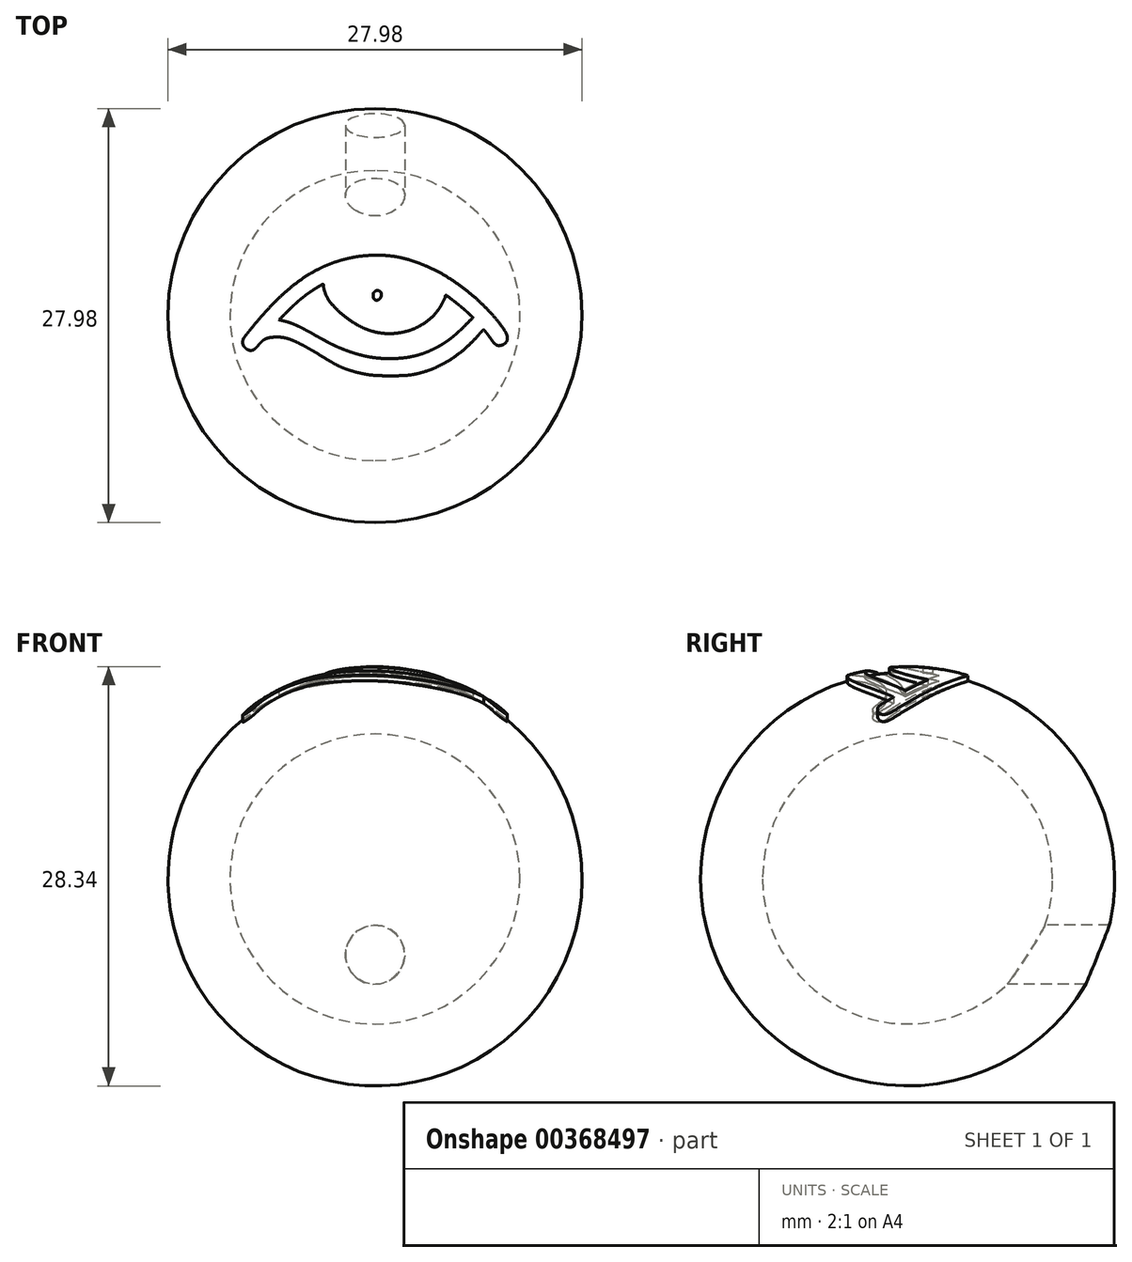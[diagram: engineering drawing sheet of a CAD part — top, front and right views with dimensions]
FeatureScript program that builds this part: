
annotation { "Feature Type Name" : "Feature", "Feature Type Description" : "" }
export const myFeature = defineFeature(function(context is Context, id is Id, definition is map)
    precondition{}
    {
        {
            var Q0;
            Q0=qCreatedBy(makeId("Top.planeOp"),FACE);
            var sketch = newSketch(context, id + "F0", { "sketchPlane" : qUnion([Q0])});
            skLineSegment(sketch, "E0", {"start": v(0, -10) * mm, "end": v(0, 10) * mm});
            skArc(sketch, "E1", {"start": v(0, 10) * mm, "mid": v(-10, 0) * mm, "end": v(0, -10) * mm});
            skSolve(sketch);
        }
        {
            var Q0;
            {var subQ0=sQuery(id+"F0.wireOp",EDGE,"E1");Q0=makeQuery(id+"F0.imprint","IMPRINT",FACE,{"disambiguationData":[TD([[makeQuery(id+"F0.imprint","IMPRINT",EDGE,{"derivedFrom":subQ0}),1.0]])]});}
            var Q1;
            Q1=sQuery(id+"F0.wireOp",EDGE,"E0");
            revolve(context, id + "F1", {"entities" : qUnion([Q0]), "axis" : qUnion([Q1]), "revolveType" : RevolveType.FULL});
        }
        {
            var Q0;
            Q0=makeQuery(id+"F1.opRevolve","SWEPT_BODY",BODY,{"disambiguationData":[OSD([sQuery(id+"F0.wireOp",EDGE,"E0"),sQuery(id+"F0.wireOp",EDGE,"E1")])]});
            var Q1;
            Q1=sQuery(id+"F0.wireOp",VERTEX,"NPe4G0ez-t7S9-9isL-QO5v-uuJu600mHcIT.center");
            var Q2;
            Q2=sQuery(id+"F0.wireOp",VERTEX,"E1.center");
            transform(context, id + "F2", {"entities" : qUnion([Q0]), "transformType" : TransformType.SCALE_UNIFORMLY, "scale" : 33.3, "scalePoint" : qUnion([Q2]), "makeCopy" : false});
        }
        {
            var Q0;
            Q0=qCreatedBy(makeId("Top.planeOp"),FACE);
            var sketch = newSketch(context, id + "F3", { "sketchPlane" : qUnion([Q0])});
            skArc(sketch, "E2", {"start": v(-15.7, 96.27) * mm, "mid": v(-24.88, 95.28) * mm, "end": v(-34, 93.81) * mm});
            skArc(sketch, "E3", {"start": v(-34, 93.81) * mm, "mid": v(-43.55, 91.8) * mm, "end": v(-53.01, 89.37) * mm});
            skArc(sketch, "E4", {"start": v(-53.01, 89.37) * mm, "mid": v(-62.4, 86.52) * mm, "end": v(-71.64, 83.27) * mm});
            skArc(sketch, "E5", {"start": v(-71.64, 83.27) * mm, "mid": v(-80.3, 79.75) * mm, "end": v(-88.77, 75.81) * mm});
            skArc(sketch, "E6", {"start": v(-88.77, 75.81) * mm, "mid": v(-102.81, 68.2) * mm, "end": v(-116.28, 59.63) * mm});
            skArc(sketch, "E7", {"start": v(-116.28, 59.63) * mm, "mid": v(-129.86, 49.68) * mm, "end": v(-142.83, 38.92) * mm});
            skArc(sketch, "E8", {"start": v(-142.83, 38.92) * mm, "mid": v(-156.87, 25.88) * mm, "end": v(-170.22, 12.13) * mm});
            skArc(sketch, "E9", {"start": v(-170.22, 12.13) * mm, "mid": v(-185.55, -5) * mm, "end": v(-200.36, -22.6) * mm});
            skArc(sketch, "E10", {"start": v(-200.36, -22.6) * mm, "mid": v(-204.26, -27.4) * mm, "end": v(-208.11, -32.22) * mm});
            skArc(sketch, "E11", {"start": v(-208.11, -32.22) * mm, "mid": v(-209.68, -34.33) * mm, "end": v(-211.1, -36.54) * mm});
            skArc(sketch, "E12", {"start": v(-211.1, -36.54) * mm, "mid": v(-211.9, -38.1) * mm, "end": v(-212.43, -39.77) * mm});
            skArc(sketch, "E13", {"start": v(-212.43, -39.77) * mm, "mid": v(-212.77, -41.62) * mm, "end": v(-212.89, -43.5) * mm});
            skArc(sketch, "E14", {"start": v(-212.89, -43.5) * mm, "mid": v(-212.7, -45.36) * mm, "end": v(-212.17, -47.16) * mm});
            skArc(sketch, "E15", {"start": v(-212.17, -47.16) * mm, "mid": v(-211.25, -49.03) * mm, "end": v(-210.08, -50.75) * mm});
            skArc(sketch, "E16", {"start": v(-210.08, -50.75) * mm, "mid": v(-208.63, -52.35) * mm, "end": v(-206.98, -53.74) * mm});
            skArc(sketch, "E17", {"start": v(-206.98, -53.74) * mm, "mid": v(-205.23, -54.82) * mm, "end": v(-203.34, -55.62) * mm});
            skArc(sketch, "E18", {"start": v(-203.34, -55.62) * mm, "mid": v(-201.34, -56.09) * mm, "end": v(-199.3, -56.2) * mm});
            skArc(sketch, "E19", {"start": v(-199.3, -56.2) * mm, "mid": v(-197.43, -55.94) * mm, "end": v(-195.66, -55.27) * mm});
            skArc(sketch, "E20", {"start": v(-195.66, -55.27) * mm, "mid": v(-193.67, -54.05) * mm, "end": v(-191.9, -52.53) * mm});
            skArc(sketch, "E21", {"start": v(-191.9, -52.53) * mm, "mid": v(-189.54, -50.04) * mm, "end": v(-187.31, -47.43) * mm});
            skArc(sketch, "E22", {"start": v(-187.31, -47.43) * mm, "mid": v(-184.58, -44.29) * mm, "end": v(-181.61, -41.36) * mm});
            skArc(sketch, "E23", {"start": v(-181.61, -41.36) * mm, "mid": v(-179.01, -39.32) * mm, "end": v(-176.14, -37.68) * mm});
            skArc(sketch, "E24", {"start": v(-176.14, -37.68) * mm, "mid": v(-172.97, -36.44) * mm, "end": v(-169.65, -35.65) * mm});
            skArc(sketch, "E25", {"start": v(-169.65, -35.65) * mm, "mid": v(-165.2, -35.07) * mm, "end": v(-160.72, -34.76) * mm});
            skArc(sketch, "E26", {"start": v(-160.72, -34.76) * mm, "mid": v(-158.15, -34.7) * mm, "end": v(-155.59, -34.7) * mm});
            skArc(sketch, "E27", {"start": v(-155.59, -34.7) * mm, "mid": v(-153.46, -34.78) * mm, "end": v(-151.33, -34.94) * mm});
            skArc(sketch, "E28", {"start": v(-151.33, -34.94) * mm, "mid": v(-149.29, -35.18) * mm, "end": v(-147.26, -35.51) * mm});
            skArc(sketch, "E29", {"start": v(-147.26, -35.51) * mm, "mid": v(-144.98, -35.98) * mm, "end": v(-142.72, -36.5) * mm});
            skArc(sketch, "E30", {"start": v(-142.72, -36.5) * mm, "mid": v(-137.7, -37.98) * mm, "end": v(-132.83, -39.85) * mm});
            skArc(sketch, "E31", {"start": v(-132.83, -39.85) * mm, "mid": v(-126.18, -42.83) * mm, "end": v(-119.62, -46) * mm});
            skArc(sketch, "E32", {"start": v(-119.62, -46) * mm, "mid": v(-111.94, -50) * mm, "end": v(-104.36, -54.22) * mm});
            skArc(sketch, "E33", {"start": v(-104.36, -54.22) * mm, "mid": v(-96.08, -59.09) * mm, "end": v(-87.89, -64.12) * mm});
            skArc(sketch, "E34", {"start": v(-87.89, -64.12) * mm, "mid": v(-78.64, -69.83) * mm, "end": v(-69.3, -75.4) * mm});
            skArc(sketch, "E35", {"start": v(-69.3, -75.4) * mm, "mid": v(-62.78, -79.02) * mm, "end": v(-56.09, -82.33) * mm});
            skArc(sketch, "E36", {"start": v(-56.09, -82.33) * mm, "mid": v(-50.08, -84.92) * mm, "end": v(-43.94, -87.15) * mm});
            skArc(sketch, "E37", {"start": v(-43.94, -87.15) * mm, "mid": v(-36.7, -89.4) * mm, "end": v(-29.39, -91.38) * mm});
            skArc(sketch, "E38", {"start": v(-29.39, -91.38) * mm, "mid": v(-22.75, -92.95) * mm, "end": v(-16.08, -94.33) * mm});
            skArc(sketch, "E39", {"start": v(-16.08, -94.33) * mm, "mid": v(-10.4, -95.3) * mm, "end": v(-4.68, -96.02) * mm});
            skArc(sketch, "E40", {"start": v(-4.68, -96.02) * mm, "mid": v(1.7, -96.55) * mm, "end": v(8.07, -96.83) * mm});
            skArc(sketch, "E41", {"start": v(8.07, -96.83) * mm, "mid": v(17.1, -97) * mm, "end": v(26.11, -97.06) * mm});
            skArc(sketch, "E42", {"start": v(26.11, -97.06) * mm, "mid": v(34.81, -96.98) * mm, "end": v(43.5, -96.78) * mm});
            skArc(sketch, "E43", {"start": v(43.5, -96.78) * mm, "mid": v(49.38, -96.48) * mm, "end": v(55.24, -95.93) * mm});
            skArc(sketch, "E44", {"start": v(55.24, -95.93) * mm, "mid": v(60.42, -95.18) * mm, "end": v(65.57, -94.17) * mm});
            skArc(sketch, "E45", {"start": v(65.57, -94.17) * mm, "mid": v(71.73, -92.68) * mm, "end": v(77.85, -91.01) * mm});
            skArc(sketch, "E46", {"start": v(77.85, -91.01) * mm, "mid": v(89.65, -87.08) * mm, "end": v(101.1, -82.22) * mm});
            skArc(sketch, "E47", {"start": v(101.1, -82.22) * mm, "mid": v(112.52, -76.3) * mm, "end": v(123.5, -69.56) * mm});
            skArc(sketch, "E48", {"start": v(123.5, -69.56) * mm, "mid": v(134.48, -61.7) * mm, "end": v(144.89, -53.1) * mm});
            skArc(sketch, "E49", {"start": v(144.89, -53.1) * mm, "mid": v(155.3, -43.34) * mm, "end": v(165.12, -32.98) * mm});
            skLineSegment(sketch, "E50", {"start": v(165.12, -32.98) * mm, "end": v(174.6, -22.4) * mm});
            skLineSegment(sketch, "E51", {"start": v(174.6, -22.4) * mm, "end": v(177.93, -26.25) * mm});
            skArc(sketch, "E52", {"start": v(177.93, -26.25) * mm, "mid": v(178.76, -27.23) * mm, "end": v(179.56, -28.24) * mm});
            skArc(sketch, "E53", {"start": v(179.56, -28.24) * mm, "mid": v(180.69, -29.73) * mm, "end": v(181.8, -31.22) * mm});
            skArc(sketch, "E54", {"start": v(181.8, -31.22) * mm, "mid": v(183.01, -32.88) * mm, "end": v(184.21, -34.54) * mm});
            skArc(sketch, "E55", {"start": v(184.21, -34.54) * mm, "mid": v(185.33, -36.15) * mm, "end": v(186.44, -37.76) * mm});
            skArc(sketch, "E56", {"start": v(186.44, -37.76) * mm, "mid": v(188.89, -41.17) * mm, "end": v(191.53, -44.43) * mm});
            skArc(sketch, "E57", {"start": v(191.53, -44.43) * mm, "mid": v(193.5, -46.3) * mm, "end": v(195.78, -47.72) * mm});
            skArc(sketch, "E58", {"start": v(195.78, -47.72) * mm, "mid": v(197.94, -48.43) * mm, "end": v(200.2, -48.52) * mm});
            skArc(sketch, "E59", {"start": v(200.2, -48.52) * mm, "mid": v(202.97, -48.04) * mm, "end": v(205.62, -47.16) * mm});
            skArc(sketch, "E60", {"start": v(205.62, -47.16) * mm, "mid": v(208.3, -45.62) * mm, "end": v(210.53, -43.46) * mm});
            skArc(sketch, "E61", {"start": v(210.53, -43.46) * mm, "mid": v(212.04, -40.9) * mm, "end": v(212.79, -38.01) * mm});
            skArc(sketch, "E62", {"start": v(212.79, -38.01) * mm, "mid": v(212.79, -34.58) * mm, "end": v(212.02, -31.24) * mm});
            skArc(sketch, "E63", {"start": v(212.02, -31.24) * mm, "mid": v(210.38, -27.4) * mm, "end": v(208.26, -23.82) * mm});
            skArc(sketch, "E64", {"start": v(208.26, -23.82) * mm, "mid": v(196.57, -8.01) * mm, "end": v(183.65, 6.8) * mm});
            skArc(sketch, "E65", {"start": v(183.65, 6.8) * mm, "mid": v(168.5, 21.85) * mm, "end": v(152.44, 35.92) * mm});
            skArc(sketch, "E66", {"start": v(152.44, 35.92) * mm, "mid": v(135.48, 49) * mm, "end": v(117.73, 60.98) * mm});
            skArc(sketch, "E67", {"start": v(117.73, 60.98) * mm, "mid": v(100.55, 70.9) * mm, "end": v(82.64, 79.43) * mm});
            skArc(sketch, "E68", {"start": v(82.64, 79.43) * mm, "mid": v(70.04, 84.47) * mm, "end": v(57.22, 88.9) * mm});
            skArc(sketch, "E69", {"start": v(57.22, 88.9) * mm, "mid": v(45.56, 92.16) * mm, "end": v(33.7, 94.6) * mm});
            skArc(sketch, "E70", {"start": v(33.7, 94.6) * mm, "mid": v(21.92, 96.2) * mm, "end": v(10.05, 96.96) * mm});
            skArc(sketch, "E71", {"start": v(10.05, 96.96) * mm, "mid": v(-2.83, 96.97) * mm, "end": v(-15.7, 96.27) * mm});
            skArc(sketch, "E72", {"start": v(-82.87, 47.15) * mm, "mid": v(-82.82, 46.3) * mm, "end": v(-82.7, 45.47) * mm});
            skArc(sketch, "E73", {"start": v(-82.7, 45.47) * mm, "mid": v(-82.45, 44.2) * mm, "end": v(-82.17, 42.93) * mm});
            skArc(sketch, "E74", {"start": v(-82.17, 42.93) * mm, "mid": v(-81.8, 41.5) * mm, "end": v(-81.41, 40.08) * mm});
            skArc(sketch, "E75", {"start": v(-81.41, 40.08) * mm, "mid": v(-80.99, 38.7) * mm, "end": v(-80.52, 37.33) * mm});
            skArc(sketch, "E76", {"start": v(-80.52, 37.33) * mm, "mid": v(-75.98, 27.48) * mm, "end": v(-69.69, 18.65) * mm});
            skArc(sketch, "E77", {"start": v(-69.69, 18.65) * mm, "mid": v(-60.18, 8.6) * mm, "end": v(-49.8, -0.55) * mm});
            skArc(sketch, "E78", {"start": v(-49.8, -0.55) * mm, "mid": v(-38.08, -9.14) * mm, "end": v(-25.64, -16.65) * mm});
            skArc(sketch, "E79", {"start": v(-25.64, -16.65) * mm, "mid": v(-13.91, -22.11) * mm, "end": v(-1.6, -26.06) * mm});
            skArc(sketch, "E80", {"start": v(-1.6, -26.06) * mm, "mid": v(12.82, -28.6) * mm, "end": v(27.45, -29.03) * mm});
            skArc(sketch, "E81", {"start": v(27.45, -29.03) * mm, "mid": v(42.14, -27.34) * mm, "end": v(56.45, -23.6) * mm});
            skArc(sketch, "E82", {"start": v(56.45, -23.6) * mm, "mid": v(69.79, -17.97) * mm, "end": v(82.17, -10.47) * mm});
            skArc(sketch, "E83", {"start": v(82.17, -10.47) * mm, "mid": v(92.73, -1.58) * mm, "end": v(101.67, 8.94) * mm});
            skArc(sketch, "E84", {"start": v(101.67, 8.94) * mm, "mid": v(103.47, 11.6) * mm, "end": v(105.14, 14.32) * mm});
            skArc(sketch, "E85", {"start": v(105.14, 14.32) * mm, "mid": v(107.13, 17.86) * mm, "end": v(109.03, 21.44) * mm});
            skArc(sketch, "E86", {"start": v(109.03, 21.44) * mm, "mid": v(110.8, 24.92) * mm, "end": v(112.5, 28.44) * mm});
            skArc(sketch, "E87", {"start": v(112.5, 28.44) * mm, "mid": v(112.96, 29.75) * mm, "end": v(113.11, 31.12) * mm});
            skArc(sketch, "E88", {"start": v(113.11, 31.12) * mm, "mid": v(113.13, 31.37) * mm, "end": v(113.17, 31.61) * mm});
            skArc(sketch, "E89", {"start": v(113.17, 31.61) * mm, "mid": v(113.24, 31.83) * mm, "end": v(113.34, 32.03) * mm});
            skArc(sketch, "E90", {"start": v(113.34, 32.03) * mm, "mid": v(113.46, 32.18) * mm, "end": v(113.6, 32.3) * mm});
            skArc(sketch, "E91", {"start": v(113.6, 32.3) * mm, "mid": v(113.74, 32.38) * mm, "end": v(113.9, 32.4) * mm});
            skArc(sketch, "E92", {"start": v(113.9, 32.4) * mm, "mid": v(115.02, 32.21) * mm, "end": v(116.02, 31.67) * mm});
            skArc(sketch, "E93", {"start": v(116.02, 31.67) * mm, "mid": v(122.38, 26.73) * mm, "end": v(128.73, 21.77) * mm});
            skArc(sketch, "E94", {"start": v(128.73, 21.77) * mm, "mid": v(134.7, 17.03) * mm, "end": v(140.62, 12.21) * mm});
            skArc(sketch, "E95", {"start": v(140.62, 12.21) * mm, "mid": v(144.67, 8.76) * mm, "end": v(148.6, 5.17) * mm});
            skLineSegment(sketch, "E96", {"start": v(148.6, 5.17) * mm, "end": v(157.59, -3.31) * mm});
            skLineSegment(sketch, "E97", {"start": v(157.59, -3.31) * mm, "end": v(142.6, -18.24) * mm});
            skArc(sketch, "E98", {"start": v(142.6, -18.24) * mm, "mid": v(136.78, -23.9) * mm, "end": v(130.82, -29.4) * mm});
            skArc(sketch, "E99", {"start": v(130.82, -29.4) * mm, "mid": v(125.67, -33.85) * mm, "end": v(120.33, -38.08) * mm});
            skArc(sketch, "E100", {"start": v(120.33, -38.08) * mm, "mid": v(115.17, -41.8) * mm, "end": v(109.84, -45.3) * mm});
            skArc(sketch, "E101", {"start": v(109.84, -45.3) * mm, "mid": v(104.04, -48.75) * mm, "end": v(98.11, -51.97) * mm});
            skArc(sketch, "E102", {"start": v(98.11, -51.97) * mm, "mid": v(90.09, -55.89) * mm, "end": v(81.87, -59.38) * mm});
            skArc(sketch, "E103", {"start": v(81.87, -59.38) * mm, "mid": v(73.97, -62.22) * mm, "end": v(65.92, -64.57) * mm});
            skArc(sketch, "E104", {"start": v(65.92, -64.57) * mm, "mid": v(57.65, -66.43) * mm, "end": v(49.28, -67.79) * mm});
            skArc(sketch, "E105", {"start": v(49.28, -67.79) * mm, "mid": v(40.14, -68.76) * mm, "end": v(30.96, -69.3) * mm});
            skArc(sketch, "E106", {"start": v(30.96, -69.3) * mm, "mid": v(21.95, -69.42) * mm, "end": v(12.94, -69.14) * mm});
            skArc(sketch, "E107", {"start": v(12.94, -69.14) * mm, "mid": v(4.36, -68.5) * mm, "end": v(-4.18, -67.41) * mm});
            skArc(sketch, "E108", {"start": v(-4.18, -67.41) * mm, "mid": v(-12.76, -65.9) * mm, "end": v(-21.27, -63.98) * mm});
            skArc(sketch, "E109", {"start": v(-21.27, -63.98) * mm, "mid": v(-30.29, -61.5) * mm, "end": v(-39.2, -58.7) * mm});
            skArc(sketch, "E110", {"start": v(-39.2, -58.7) * mm, "mid": v(-46.15, -56.25) * mm, "end": v(-53.02, -53.62) * mm});
            skArc(sketch, "E111", {"start": v(-53.02, -53.62) * mm, "mid": v(-59.24, -51.03) * mm, "end": v(-65.37, -48.24) * mm});
            skArc(sketch, "E112", {"start": v(-65.37, -48.24) * mm, "mid": v(-72.4, -44.77) * mm, "end": v(-79.33, -41.12) * mm});
            skArc(sketch, "E113", {"start": v(-79.33, -41.12) * mm, "mid": v(-89.08, -35.75) * mm, "end": v(-98.78, -30.3) * mm});
            skArc(sketch, "E114", {"start": v(-98.78, -30.3) * mm, "mid": v(-106.38, -26.03) * mm, "end": v(-114.04, -21.88) * mm});
            skArc(sketch, "E115", {"start": v(-114.04, -21.88) * mm, "mid": v(-119.86, -18.9) * mm, "end": v(-125.78, -16.1) * mm});
            skArc(sketch, "E116", {"start": v(-125.78, -16.1) * mm, "mid": v(-130.73, -13.97) * mm, "end": v(-135.75, -12.05) * mm});
            skArc(sketch, "E117", {"start": v(-135.75, -12.05) * mm, "mid": v(-140.5, -10.48) * mm, "end": v(-145.33, -9.16) * mm});
            skLineSegment(sketch, "E118", {"start": v(-145.33, -9.16) * mm, "end": v(-154.28, -6.95) * mm});
            skLineSegment(sketch, "E119", {"start": v(-154.28, -6.95) * mm, "end": v(-140.33, 7) * mm});
            skArc(sketch, "E120", {"start": v(-140.33, 7) * mm, "mid": v(-135.38, 11.87) * mm, "end": v(-130.35, 16.68) * mm});
            skArc(sketch, "E121", {"start": v(-130.35, 16.68) * mm, "mid": v(-125.96, 20.72) * mm, "end": v(-121.47, 24.66) * mm});
            skArc(sketch, "E122", {"start": v(-121.47, 24.66) * mm, "mid": v(-117.31, 28.12) * mm, "end": v(-113.07, 31.47) * mm});
            skArc(sketch, "E123", {"start": v(-113.07, 31.47) * mm, "mid": v(-108.85, 34.62) * mm, "end": v(-104.55, 37.63) * mm});
            skArc(sketch, "E124", {"start": v(-104.55, 37.63) * mm, "mid": v(-101.45, 39.71) * mm, "end": v(-98.31, 41.75) * mm});
            skArc(sketch, "E125", {"start": v(-98.31, 41.75) * mm, "mid": v(-94.91, 43.9) * mm, "end": v(-91.49, 46.02) * mm});
            skArc(sketch, "E126", {"start": v(-91.49, 46.02) * mm, "mid": v(-88.18, 48.02) * mm, "end": v(-84.86, 50.02) * mm});
            skArc(sketch, "E127", {"start": v(-84.86, 50.02) * mm, "mid": v(-84.27, 50.28) * mm, "end": v(-83.64, 50.38) * mm});
            skArc(sketch, "E128", {"start": v(-83.64, 50.38) * mm, "mid": v(-83.46, 50.33) * mm, "end": v(-83.34, 50.19) * mm});
            skArc(sketch, "E129", {"start": v(-83.34, 50.19) * mm, "mid": v(-83.2, 49.82) * mm, "end": v(-83.1, 49.44) * mm});
            skArc(sketch, "E130", {"start": v(-83.1, 49.44) * mm, "mid": v(-83, 48.92) * mm, "end": v(-82.93, 48.4) * mm});
            skArc(sketch, "E131", {"start": v(-82.93, 48.4) * mm, "mid": v(-82.88, 47.77) * mm, "end": v(-82.87, 47.15) * mm});
            skArc(sketch, "E132", {"start": v(7.9, 38.84) * mm, "mid": v(8.45, 38.4) * mm, "end": v(8.95, 37.88) * mm});
            skArc(sketch, "E133", {"start": v(8.95, 37.88) * mm, "mid": v(9.33, 37.35) * mm, "end": v(9.63, 36.75) * mm});
            skArc(sketch, "E134", {"start": v(9.63, 36.75) * mm, "mid": v(9.86, 36.04) * mm, "end": v(10, 35.3) * mm});
            skArc(sketch, "E135", {"start": v(10, 35.3) * mm, "mid": v(10.08, 34.3) * mm, "end": v(10.11, 33.3) * mm});
            skArc(sketch, "E136", {"start": v(10.11, 33.3) * mm, "mid": v(9.67, 30.37) * mm, "end": v(8.37, 27.7) * mm});
            skArc(sketch, "E137", {"start": v(8.37, 27.7) * mm, "mid": v(6.42, 25.77) * mm, "end": v(3.9, 24.69) * mm});
            skArc(sketch, "E138", {"start": v(3.9, 24.69) * mm, "mid": v(1.5, 24.73) * mm, "end": v(-0.63, 25.85) * mm});
            skArc(sketch, "E139", {"start": v(-0.63, 25.85) * mm, "mid": v(-2.2, 27.9) * mm, "end": v(-2.9, 30.4) * mm});
            skArc(sketch, "E140", {"start": v(-2.9, 30.4) * mm, "mid": v(-3, 31.9) * mm, "end": v(-3.03, 33.4) * mm});
            skArc(sketch, "E141", {"start": v(-3.03, 33.4) * mm, "mid": v(-2.96, 34.37) * mm, "end": v(-2.77, 35.32) * mm});
            skArc(sketch, "E142", {"start": v(-2.77, 35.32) * mm, "mid": v(-2.47, 36.1) * mm, "end": v(-2.05, 36.83) * mm});
            skArc(sketch, "E143", {"start": v(-2.05, 36.83) * mm, "mid": v(-1.4, 37.63) * mm, "end": v(-0.7, 38.36) * mm});
            skArc(sketch, "E144", {"start": v(-0.7, 38.36) * mm, "mid": v(0.26, 39.13) * mm, "end": v(1.32, 39.75) * mm});
            skArc(sketch, "E145", {"start": v(1.32, 39.75) * mm, "mid": v(2.35, 40.14) * mm, "end": v(3.44, 40.31) * mm});
            skArc(sketch, "E146", {"start": v(3.44, 40.31) * mm, "mid": v(4.56, 40.26) * mm, "end": v(5.64, 40) * mm});
            skArc(sketch, "E147", {"start": v(5.64, 40) * mm, "mid": v(6.8, 39.5) * mm, "end": v(7.9, 38.84) * mm});
            skSolve(sketch);
        }
        {
            var Q0;
            Q0=qSketchRegion(id+"F3",true);
            var Q1;
            Q1=sQuery(id+"F3.wireOp",EDGE,"c928f899-12af-4b01-b412-b3b7da3d830f");
            var Q2;
            Q2=sQuery(id+"F3.wireOp",EDGE,"b69f99c7-a6d0-4d1b-8752-9e82ab4c99ec");
            extrude(context, id + "F4", {"entities" : qUnion([Q0]), "operationType" : NewBodyOperationType.ADD, "surfaceEntities" : qUnion([Q1, Q2]), "depth" : 350 * mm});
        }
        {
            var Q0;
            Q0=makeQuery(id+"F4.opExtrude","SWEPT_BODY",BODY,{"disambiguationData":[OSD([sQuery(id+"F3.wireOp",EDGE,"15c6da4e-992d-4824-9d20-70d2d6be9970"),sQuery(id+"F3.wireOp",EDGE,"268c69ec-46be-456f-85eb-69decc32fe39"),sQuery(id+"F3.wireOp",EDGE,"1d386307-6059-4203-bca6-0c1cec3c82e1"),sQuery(id+"F3.wireOp",EDGE,"7d7c66d2-f869-427f-806b-ad436cacd60e"),sQuery(id+"F3.wireOp",EDGE,"1db91850-860e-493f-a3af-7a0f3f1512ae"),sQuery(id+"F3.wireOp",EDGE,"2c65f23b-9f03-4f6f-ab37-de452af29e3c"),sQuery(id+"F3.wireOp",EDGE,"ba006cbc-bbd7-44d9-84cc-9cde0967c280"),sQuery(id+"F3.wireOp",EDGE,"ae950208-c781-4a25-8fcf-ffe59b9085ff"),sQuery(id+"F3.wireOp",EDGE,"3cce0944-c62d-4831-9b9d-d1a418d328b4"),sQuery(id+"F3.wireOp",EDGE,"9edc5e7d-16c0-40c4-98ad-6b91d5df0e78"),sQuery(id+"F3.wireOp",EDGE,"aa452f44-44a2-4c64-bff5-a2a639df00db"),sQuery(id+"F3.wireOp",EDGE,"16259f99-ce20-4b7b-81e1-fa0909c03eb4"),sQuery(id+"F3.wireOp",EDGE,"79895566-a943-429d-b257-d76af3645bdf"),sQuery(id+"F3.wireOp",EDGE,"a85490ef-f17e-45c8-b92b-28215162778a"),sQuery(id+"F3.wireOp",EDGE,"322f1036-a6fd-4992-ab69-5919540af7a6"),sQuery(id+"F3.wireOp",EDGE,"0a87ff38-4ab4-4140-b3c3-2d7501d9f3b1"),sQuery(id+"F3.wireOp",EDGE,"a6e7bdf2-ef3e-49d4-9b3c-e34f5a41e0c4"),sQuery(id+"F3.wireOp",EDGE,"3e588790-576f-47c1-9730-f5e27fa1e8f9"),sQuery(id+"F3.wireOp",EDGE,"ce3739ef-15fd-4754-ad9c-ccf511a9a8fb"),sQuery(id+"F3.wireOp",EDGE,"201134a3-66f3-4a3f-aa9b-76948966efc0"),sQuery(id+"F3.wireOp",EDGE,"65b511ea-0759-428d-8070-88e1f521d8ea"),sQuery(id+"F3.wireOp",EDGE,"c37cddb6-5cf8-4891-aff4-7191a72080b9"),sQuery(id+"F3.wireOp",EDGE,"52a43dbd-e952-43e1-be3d-d70e107260e6"),sQuery(id+"F3.wireOp",EDGE,"08c1271f-f5c3-4f26-be27-7f5e21217dff"),sQuery(id+"F3.wireOp",EDGE,"59a09f58-0503-4180-962a-e04db21f0da8"),sQuery(id+"F3.wireOp",EDGE,"e56a4626-e956-42c3-bb5d-cd9dae1ca801"),sQuery(id+"F3.wireOp",EDGE,"5ff5d55f-af90-49eb-8040-353101557de8"),sQuery(id+"F3.wireOp",EDGE,"0ed7430b-e164-4f56-8af9-4534524aa7c0"),sQuery(id+"F3.wireOp",EDGE,"b5610a6e-b6bb-43e3-9a8d-d3d7c5f0098b"),sQuery(id+"F3.wireOp",EDGE,"1d417af8-88ad-47c2-a4e2-6fec82bd6695"),sQuery(id+"F3.wireOp",EDGE,"778ae99a-956a-4ddb-8078-d9bc57f9fc8e"),sQuery(id+"F3.wireOp",EDGE,"5b19af09-f144-446e-9dfa-8766819c9efd"),sQuery(id+"F3.wireOp",EDGE,"028339f6-0475-4a57-af8d-550e32ad7466"),sQuery(id+"F3.wireOp",EDGE,"d5ae35b6-d210-433a-92c8-e92622696872"),sQuery(id+"F3.wireOp",EDGE,"16a2e606-2caa-4876-9ffa-8f08c4ff3a37"),sQuery(id+"F3.wireOp",EDGE,"5b90b144-be56-4de7-a9dd-c1e0336acbe3"),sQuery(id+"F3.wireOp",EDGE,"5912d126-c5fc-41e4-bfb8-b4fefc52ca72"),sQuery(id+"F3.wireOp",EDGE,"2e96ce95-bd3e-4f27-a7f8-b62cf5efe954"),sQuery(id+"F3.wireOp",EDGE,"ecb4e259-1207-4dd0-bc3c-87c6506cc3a5"),sQuery(id+"F3.wireOp",EDGE,"105fb72e-4d79-4204-af2f-b3b26f5eb8d1"),sQuery(id+"F3.wireOp",EDGE,"fa59b598-df54-48c6-bb8f-c5f7618c69d0"),sQuery(id+"F3.wireOp",EDGE,"a6beef0d-f124-47ac-b957-e6cd3057a354"),sQuery(id+"F3.wireOp",EDGE,"7c3eaf53-dcb7-43b1-ad18-80ff953eb59e"),sQuery(id+"F3.wireOp",EDGE,"281fe206-104f-408f-94b6-be79f12604c9")])]});
            var Q1;
            Q1=makeQuery(id+"F4.opExtrude","SWEPT_BODY",BODY,{"disambiguationData":[OSD([sQuery(id+"F3.wireOp",EDGE,"58f6206a-5554-41d4-8cf7-6e0b4724a469"),sQuery(id+"F3.wireOp",EDGE,"85dabe77-b6aa-43d5-a519-64383616f71e"),sQuery(id+"F3.wireOp",EDGE,"4b679fe6-9e11-497d-b8fd-14ca14e49ddd"),sQuery(id+"F3.wireOp",EDGE,"51de25f6-d59e-4805-a327-1fd7e38869c8"),sQuery(id+"F3.wireOp",EDGE,"d47977fb-70d3-4df8-bc35-66fcc0e556e0"),sQuery(id+"F3.wireOp",EDGE,"235006b0-8f14-4ca2-82f0-f96b6b8c4766"),sQuery(id+"F3.wireOp",EDGE,"0fc7acd6-1c1d-47a8-ba12-62eb658d35ca"),sQuery(id+"F3.wireOp",EDGE,"883fa5e3-ca4c-4ce6-a249-4debf538fe24"),sQuery(id+"F3.wireOp",EDGE,"1da09ed1-22d9-43a1-a655-8acff5d61309"),sQuery(id+"F3.wireOp",EDGE,"32654a82-a09a-444f-bf73-45f818f0f235"),sQuery(id+"F3.wireOp",EDGE,"a398fd80-a0a9-4724-ba0e-1a7a000baa92"),sQuery(id+"F3.wireOp",EDGE,"f39f97c8-53f5-4046-9905-b28daecd4f10"),sQuery(id+"F3.wireOp",EDGE,"2484d883-0ec2-4c7d-9023-165ebbef226c"),sQuery(id+"F3.wireOp",EDGE,"f026d96f-3d32-4113-a1c9-3545f5cdbe4a"),sQuery(id+"F3.wireOp",EDGE,"974fee18-719e-4620-aace-d3676da2011b"),sQuery(id+"F3.wireOp",EDGE,"0c5766d2-a026-45af-bffd-0d1f783d5157"),sQuery(id+"F3.wireOp",EDGE,"5da13fee-9c04-45d8-805f-c7a03dde2383"),sQuery(id+"F3.wireOp",EDGE,"dbea32a3-85bd-4957-aef2-b6fe64a02f6b"),sQuery(id+"F3.wireOp",EDGE,"fba134ea-bf40-4191-ad8f-cc6b2b040a97"),sQuery(id+"F3.wireOp",EDGE,"0c19e200-7cd5-4fcb-83ed-261bd7936bc7"),sQuery(id+"F3.wireOp",EDGE,"246b843b-ea86-44e5-9cb9-335e6677b61d"),sQuery(id+"F3.wireOp",EDGE,"c1b3c9bc-1eb4-4c9b-99c8-0cebed89395a"),sQuery(id+"F3.wireOp",EDGE,"f93eebc3-1447-4029-8362-91325193ac2b"),sQuery(id+"F3.wireOp",EDGE,"bf86b12d-53a9-4c19-abaa-b1e658933ceb"),sQuery(id+"F3.wireOp",EDGE,"89646a71-1a60-4e14-b80a-74fb601d0855"),sQuery(id+"F3.wireOp",EDGE,"7b03dcde-0a52-4f3c-80e9-110d1d805e93"),sQuery(id+"F3.wireOp",EDGE,"83e8d1f3-8820-485b-8b6d-3ecd79124883"),sQuery(id+"F3.wireOp",EDGE,"ec7b56eb-ca95-44fd-a774-e9b7f9d3f50d"),sQuery(id+"F3.wireOp",EDGE,"31861aa6-cfd1-43ce-a7c5-bacfb7e2a30f"),sQuery(id+"F3.wireOp",EDGE,"fa3de647-1dd9-4141-982b-74ae8d07851d"),sQuery(id+"F3.wireOp",EDGE,"75d7c1c5-761c-4178-bfd4-4f469045899b"),sQuery(id+"F3.wireOp",EDGE,"4b3d7518-bd5d-4ecc-b2c5-d8dd665de4f4"),sQuery(id+"F3.wireOp",EDGE,"3be2682d-01bd-4f31-9cde-9df16a01e4a9"),sQuery(id+"F3.wireOp",EDGE,"72d3c7a9-2794-46eb-9b0d-6c526cc1b9a3"),sQuery(id+"F3.wireOp",EDGE,"0137e336-6b26-4f8d-b9ad-47ce1aa9eb31"),sQuery(id+"F3.wireOp",EDGE,"96000e4a-2d86-4b9f-af7d-a1c875cc048c"),sQuery(id+"F3.wireOp",EDGE,"139c5a79-9c0f-4e15-b57f-4c09662495a3"),sQuery(id+"F3.wireOp",EDGE,"8ea04d8b-b3da-46bb-9742-d8cba6b23bda"),sQuery(id+"F3.wireOp",EDGE,"b352b580-467e-481c-88ac-6217b8462947"),sQuery(id+"F3.wireOp",EDGE,"2503a493-1722-4539-8d54-7329fc0b116a"),sQuery(id+"F3.wireOp",EDGE,"a0615e06-0a48-4c65-8818-f0f693937022"),sQuery(id+"F3.wireOp",EDGE,"08389002-1ce8-438a-b5a4-698ca33590c2"),sQuery(id+"F3.wireOp",EDGE,"1756e4aa-c30a-461e-962c-81ee35d31e55"),sQuery(id+"F3.wireOp",EDGE,"5f84c249-07ea-4efb-9be3-ca494937f772"),sQuery(id+"F3.wireOp",EDGE,"cbefd041-b54f-4587-87b6-437b2290d1fc"),sQuery(id+"F3.wireOp",EDGE,"d44f58d4-f1a7-4aec-b016-8e7f1e498aeb"),sQuery(id+"F3.wireOp",EDGE,"0a5be90b-7545-44ea-9f2d-c726a5a2121c"),sQuery(id+"F3.wireOp",EDGE,"0cfaa442-d102-4580-8ef6-489f2aa1e6b3")])]});
            var Q2;
            Q2=makeQuery(id+"F4.opExtrude","SWEPT_BODY",BODY,{"disambiguationData":[OSD([sQuery(id+"F3.wireOp",EDGE,"9cc7aec6-4d94-4577-ab6c-32f5aa316238"),sQuery(id+"F3.wireOp",EDGE,"5ab2d840-4a32-405a-8c4b-a8126e3e1bc1"),sQuery(id+"F3.wireOp",EDGE,"56de48b4-9620-4637-8196-310e2641530f"),sQuery(id+"F3.wireOp",EDGE,"55327826-e64b-4830-85f2-3f22d36f43b5"),sQuery(id+"F3.wireOp",EDGE,"0245b46f-a639-4a95-8ca3-1568736ceed2"),sQuery(id+"F3.wireOp",EDGE,"9bd8a002-6ca7-4c84-8984-a620eefad103"),sQuery(id+"F3.wireOp",EDGE,"d4736c5e-da0b-46a0-ba9d-17ae07bb2b66"),sQuery(id+"F3.wireOp",EDGE,"125695b8-77e6-4e99-8f78-5f8fae1a0c71"),sQuery(id+"F3.wireOp",EDGE,"c9f25b10-a495-4684-8f25-8f255fabab6e"),sQuery(id+"F3.wireOp",EDGE,"0dbee67a-2ab6-4abb-ae16-0fe64d623848"),sQuery(id+"F3.wireOp",EDGE,"92c08d8e-ed2e-41a3-9c1a-b5ddaf8a0bf1"),sQuery(id+"F3.wireOp",EDGE,"00fabb15-0c1e-492e-85c1-17390e5b12bc"),sQuery(id+"F3.wireOp",EDGE,"065a9352-dddb-4e3f-b02a-444c867b75fe"),sQuery(id+"F3.wireOp",EDGE,"ef206bb6-e4f2-4189-9fc7-a7823c329ad6"),sQuery(id+"F3.wireOp",EDGE,"7199cbbe-c9bf-4cb9-b928-2ff8a84eb09e"),sQuery(id+"F3.wireOp",EDGE,"17bf9ed1-b881-4f74-816d-3511b6b328c7"),sQuery(id+"F3.wireOp",EDGE,"e5b615d0-4193-495d-b285-bd69ae30f000"),sQuery(id+"F3.wireOp",EDGE,"cfeaf62f-6be1-426b-9732-01e1a667be7e"),sQuery(id+"F3.wireOp",EDGE,"ac56344b-5ee6-4fa5-8e47-65b2a4ea3a01"),sQuery(id+"F3.wireOp",EDGE,"45b5fa53-15fd-43a0-91b0-943cc3286fc9")])]});
            var Q3;
            Q3=makeQuery(id+"F4.opExtrude","SWEPT_BODY",BODY,{"disambiguationData":[OSD([sQuery(id+"F3.wireOp",EDGE,"7bdfe37d-9957-4663-8239-5490fd3220d9"),sQuery(id+"F3.wireOp",EDGE,"6a91314f-c002-4565-bbf8-bb9f29165fb8"),sQuery(id+"F3.wireOp",EDGE,"b69f99c7-a6d0-4d1b-8752-9e82ab4c99ec"),sQuery(id+"F3.wireOp",EDGE,"c928f899-12af-4b01-b412-b3b7da3d830f"),sQuery(id+"F3.wireOp",EDGE,"ffa58721-cdd5-406d-be26-d96f7a050df4"),sQuery(id+"F3.wireOp",EDGE,"02fc7fb8-293b-44ff-ab78-63506d0aedb9"),sQuery(id+"F3.wireOp",EDGE,"147fb6cb-2565-4fb5-9280-6afbf9eef36b"),sQuery(id+"F3.wireOp",EDGE,"2cee3704-4124-415a-b391-31af1cf305d7"),sQuery(id+"F3.wireOp",EDGE,"32b2fb71-03c8-4978-9d95-2b5aaf044d0d"),sQuery(id+"F3.wireOp",EDGE,"e5d05796-7d6c-4350-8a4e-d55f5ade2f77"),sQuery(id+"F3.wireOp",EDGE,"77b1164c-8dd4-4680-b616-ac151a422eb2"),sQuery(id+"F3.wireOp",EDGE,"ec0798b8-0fbb-49ea-9766-39d2ee0936b0"),sQuery(id+"F3.wireOp",EDGE,"c4af6478-2a03-47a6-862f-c0c71886b8a3"),sQuery(id+"F3.wireOp",EDGE,"1912a38f-fa28-45c6-ab33-84cac2787056"),sQuery(id+"F3.wireOp",EDGE,"5d79fa95-f66d-4d2b-923b-4d54735f1fbd"),sQuery(id+"F3.wireOp",EDGE,"2db7aef4-a710-4bcf-9c1c-a8a87719953d"),sQuery(id+"F3.wireOp",EDGE,"183449de-345c-4115-9bca-43a403e62dbd"),sQuery(id+"F3.wireOp",EDGE,"e3ac8c9b-cab5-44b0-ad81-0e2b680c384a"),sQuery(id+"F3.wireOp",EDGE,"92e85db6-f458-41f6-a9a1-1e1a1a7e7809"),sQuery(id+"F3.wireOp",EDGE,"f0dbb46f-43a9-447b-9c75-8dfc9b95470d"),sQuery(id+"F3.wireOp",EDGE,"4b73f5f6-f769-4414-bdba-7d253e58fff4"),sQuery(id+"F3.wireOp",EDGE,"a88669dc-35b3-46bb-964f-c9bf6c4ab898"),sQuery(id+"F3.wireOp",EDGE,"2c559bae-f38f-4377-91e6-3c9de70acf11"),sQuery(id+"F3.wireOp",EDGE,"c1caf99b-adaa-42fe-a319-8cbcd819cf89"),sQuery(id+"F3.wireOp",EDGE,"54b04dd4-0ec4-4956-b19c-1141095738e3"),sQuery(id+"F3.wireOp",EDGE,"098f7a84-b7b8-4879-b21a-5c38879e4110"),sQuery(id+"F3.wireOp",EDGE,"b406a8e6-a226-4f3d-ac30-e4d06e4dac62"),sQuery(id+"F3.wireOp",EDGE,"36f95d1d-68ce-4231-ad71-3960c85e5915"),sQuery(id+"F3.wireOp",EDGE,"dc12cad8-2eed-454e-aa74-30099b1c9064"),sQuery(id+"F3.wireOp",EDGE,"4c78a4fd-cd81-43d6-85d6-6e4d3fbc1e98"),sQuery(id+"F3.wireOp",EDGE,"ee9e30de-787b-4e8f-b425-43a8e9289f81"),sQuery(id+"F3.wireOp",EDGE,"2518a3a4-c96b-4463-8704-0b71c65c60d2"),sQuery(id+"F3.wireOp",EDGE,"c9129a67-398c-4e37-92cb-2d54ff2e2e82"),sQuery(id+"F3.wireOp",EDGE,"d429d547-9f5b-42c6-bcca-effad2fa908f"),sQuery(id+"F3.wireOp",EDGE,"99d16e94-b2b3-43d5-9c7b-7bd463994dcb"),sQuery(id+"F3.wireOp",EDGE,"32993909-9a70-47ee-9097-89fff220f839"),sQuery(id+"F3.wireOp",EDGE,"6eabbeed-9496-4825-b168-63782a34f495"),sQuery(id+"F3.wireOp",EDGE,"f74987e3-8e60-4a5b-857f-839ae8aaf0cf"),sQuery(id+"F3.wireOp",EDGE,"1c218c86-035d-4441-93c0-9621d3297c3a"),sQuery(id+"F3.wireOp",EDGE,"0133f513-4b11-4cc4-b075-4625e9591e41"),sQuery(id+"F3.wireOp",EDGE,"fe921ad4-a8f5-4772-9aeb-350aca2e8948"),sQuery(id+"F3.wireOp",EDGE,"bfde0a4f-3cec-4f8e-8a23-dd1441b34c2b"),sQuery(id+"F3.wireOp",EDGE,"b41521ff-c5df-4b64-83ed-5e7635cf4438"),sQuery(id+"F3.wireOp",EDGE,"ed692599-6bbb-4379-8e89-ea326a0a0f87"),sQuery(id+"F3.wireOp",EDGE,"a98451c0-d76c-436e-99f9-a3fe9c8430a4"),sQuery(id+"F3.wireOp",EDGE,"561965b2-3050-4f49-9305-d98a2b852bbe"),sQuery(id+"F3.wireOp",EDGE,"e13dfa59-48e6-4b4e-94b9-1fc5254b0f2e"),sQuery(id+"F3.wireOp",EDGE,"0354e106-253a-4bfa-b5b7-b09cd0f2f6c0"),sQuery(id+"F3.wireOp",EDGE,"8df1dcc8-d00a-4777-85fd-8af8e9830bd1"),sQuery(id+"F3.wireOp",EDGE,"26ce3762-0d1a-4b81-9a23-debcfc24da1c"),sQuery(id+"F3.wireOp",EDGE,"3e900f8f-3ffb-4e32-b536-61fea2f3e30a"),sQuery(id+"F3.wireOp",EDGE,"4a1b5445-5559-461f-b6f1-b4cd9b95ea10")])]});
            var Q4;
            Q4=makeQuery(id+"F1.opRevolve","SWEPT_BODY",BODY,{"disambiguationData":[OSD([sQuery(id+"F0.wireOp",EDGE,"E0"),sQuery(id+"F0.wireOp",EDGE,"E1")])]});
            var Q5;
            Q5=qCreatedBy(makeId("Origin.pointOp"),VERTEX);
            transform(context, id + "F5", {"entities" : qUnion([Q0, Q1, Q2, Q3, Q4]), "transformType" : TransformType.SCALE_UNIFORMLY, "scale" : 0.03, "scalePoint" : qUnion([Q5]), "makeCopy" : false});
        }
        {
            var Q0;
            Q0=qCreatedBy(makeId("Top.planeOp"),FACE);
            var sketch = newSketch(context, id + "F6", { "sketchPlane" : qUnion([Q0])});
            skLineSegment(sketch, "E148", {"start": v(0, 15) * mm, "end": v(0, -15) * mm});
            skArc(sketch, "E149", {"start": v(0, 15) * mm, "mid": v(-15, 0) * mm, "end": v(0, -15) * mm});
            skArc(sketch, "E150", {"start": v(0, 10.25) * mm, "mid": v(-10.25, 0) * mm, "end": v(0, -10.25) * mm});
            skArc(sketch, "E151", {"start": v(0, 7) * mm, "mid": v(-7, 0) * mm, "end": v(0, -7) * mm});
            skSolve(sketch);
        }
        {
            var Q0;
            {var subQ0=sQuery(id+"F6.wireOp",EDGE,"E149");Q0=makeQuery(id+"F6.imprint","IMPRINT",FACE,{"disambiguationData":[TD([[makeQuery(id+"F6.imprint","IMPRINT",EDGE,{"derivedFrom":subQ0}),1.0]])]});}
            var Q1;
            {var subQ0=sQuery(id+"F6.wireOp",EDGE,"E151");Q1=makeQuery(id+"F6.imprint","IMPRINT",FACE,{"disambiguationData":[TD([[makeQuery(id+"F6.imprint","IMPRINT",EDGE,{"derivedFrom":subQ0}),1.0]])]});}
            var Q2;
            Q2=sQuery(id+"F6.wireOp",EDGE,"E148");
            revolve(context, id + "F7", {"operationType" : NewBodyOperationType.REMOVE, "entities" : qUnion([Q0, Q1]), "axis" : qUnion([Q2]), "revolveType" : RevolveType.FULL});
        }
        {
            var Q0;
            Q0=makeQuery(id+"F1.opRevolve","SWEPT_BODY",BODY,{"disambiguationData":[OSD([sQuery(id+"F0.wireOp",EDGE,"E0"),sQuery(id+"F0.wireOp",EDGE,"E1")])]});
            var Q1;
            Q1=sQuery(id+"F0.wireOp",VERTEX,"E1.center");
            transform(context, id + "F8", {"entities" : qUnion([Q0]), "transformType" : TransformType.SCALE_UNIFORMLY, "scale" : 1.4, "scalePoint" : qUnion([Q1]), "makeCopy" : false});
        }
        {
            var Q0;
            Q0=qCreatedBy(makeId("Front.planeOp"),FACE);
            var sketch = newSketch(context, id + "F9", { "sketchPlane" : qUnion([Q0])});
            skCircle(sketch, "E152", {"center": v(0, -5.12) * mm, "radius": 2 * mm});
            skSolve(sketch);
        }
        {
            var Q0;
            Q0=qSketchRegion(id+"F9",true);
            extrude(context, id + "F10", {"entities" : qUnion([Q0]), "operationType" : NewBodyOperationType.REMOVE, "oppositeDirection" : true, "depth" : 25 * mm});
        }
    });
